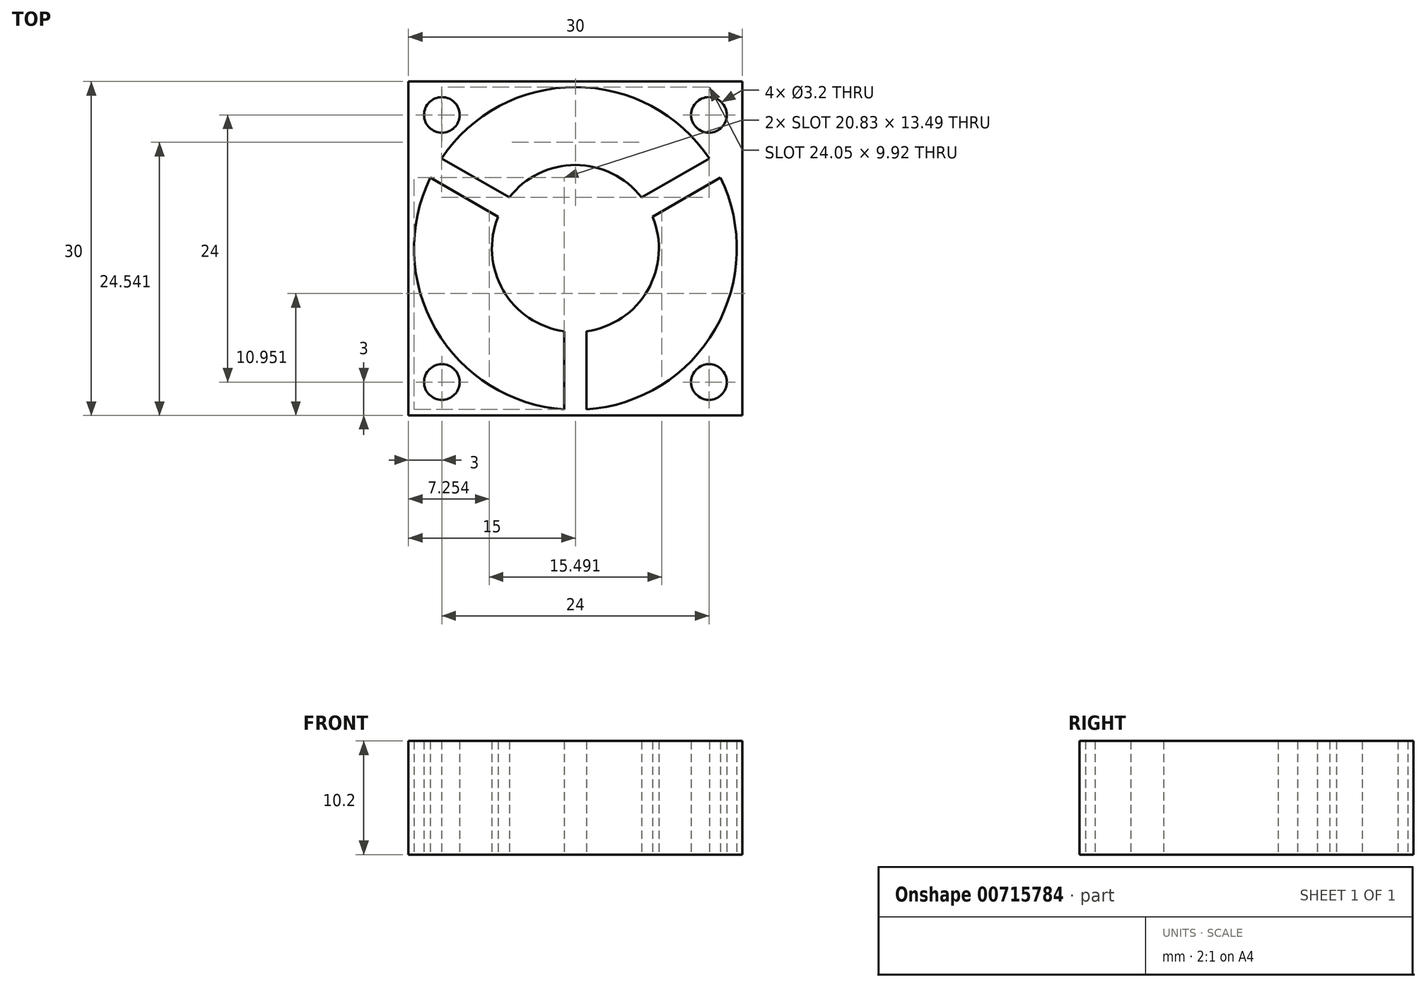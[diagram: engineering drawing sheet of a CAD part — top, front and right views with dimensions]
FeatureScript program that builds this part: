
annotation { "Feature Type Name" : "Feature", "Feature Type Description" : "" }
export const myFeature = defineFeature(function(context is Context, id is Id, definition is map)
    precondition{}
    {
        {
            var Q0;
            Q0=qCreatedBy(makeId("Top.planeOp"),FACE);
            var sketch = newSketch(context, id + "F0", { "sketchPlane" : qUnion([Q0])});
            skLineSegment(sketch, "E0.bottom", {"start": v(15, 15) * mm, "end": v(-15, 15) * mm});
            skLineSegment(sketch, "E0.top", {"start": v(15, -15) * mm, "end": v(-15, -15) * mm});
            skLineSegment(sketch, "E0.left", {"start": v(15, 15) * mm, "end": v(15, -15) * mm});
            skLineSegment(sketch, "E0.right", {"start": v(-15, 15) * mm, "end": v(-15, -15) * mm});
            skPoint(sketch, "E0.middle", {"position": v(0, 0) * mm});
            skLineSegment(sketch, "E1.bottom", {"start": v(12, 12) * mm, "end": v(-12, 12) * mm, "construction": true});
            skLineSegment(sketch, "E1.top", {"start": v(12, -12) * mm, "end": v(-12, -12) * mm, "construction": true});
            skLineSegment(sketch, "E1.left", {"start": v(12, 12) * mm, "end": v(12, -12) * mm, "construction": true});
            skLineSegment(sketch, "E1.right", {"start": v(-12, 12) * mm, "end": v(-12, -12) * mm, "construction": true});
            skCircle(sketch, "E2", {"center": v(0, 0) * mm, "radius": 14.5 * mm});
            skCircle(sketch, "E3", {"center": v(0, 0) * mm, "radius": 7.5 * mm});
            skCircle(sketch, "E4", {"center": v(-12, 12) * mm, "radius": 1.6 * mm});
            skCircle(sketch, "E5", {"center": v(12, 12) * mm, "radius": 1.6 * mm});
            skCircle(sketch, "E6", {"center": v(12, -12) * mm, "radius": 1.6 * mm});
            skCircle(sketch, "E7", {"center": v(-12, -12) * mm, "radius": 1.6 * mm});
            skLineSegment(sketch, "E8.bottom", {"start": v(1, -7.43) * mm, "end": v(-1, -7.43) * mm});
            skLineSegment(sketch, "E8.top", {"start": v(1, -14.5) * mm, "end": v(-1, -14.5) * mm});
            skLineSegment(sketch, "E8.left", {"start": v(1, -7.43) * mm, "end": v(1, -14.5) * mm});
            skLineSegment(sketch, "E8.right", {"start": v(-1, -7.43) * mm, "end": v(-1, -14.5) * mm});
            skPoint(sketch, "E8.middle", {"position": v(0, -10.97) * mm});
            skLineSegment(sketch, "E9.1.0", {"start": v(5.94, 4.58) * mm, "end": v(12.06, 8.12) * mm});
            skLineSegment(sketch, "E9.1.1", {"start": v(5.94, 4.58) * mm, "end": v(6.94, 2.85) * mm});
            skLineSegment(sketch, "E9.1.2", {"start": v(6.94, 2.85) * mm, "end": v(13.06, 6.38) * mm});
            skLineSegment(sketch, "E9.1.3", {"start": v(12.06, 8.12) * mm, "end": v(13.06, 6.38) * mm});
            skLineSegment(sketch, "E9.2.0", {"start": v(-6.94, 2.85) * mm, "end": v(-13.06, 6.38) * mm});
            skLineSegment(sketch, "E9.2.1", {"start": v(-6.94, 2.85) * mm, "end": v(-5.94, 4.58) * mm});
            skLineSegment(sketch, "E9.2.2", {"start": v(-5.94, 4.58) * mm, "end": v(-12.06, 8.12) * mm});
            skLineSegment(sketch, "E9.2.3", {"start": v(-13.06, 6.38) * mm, "end": v(-12.06, 8.12) * mm});
            skSolve(sketch);
        }
        {
            var Q0;
            Q0=makeQuery(id+"F0.imprint","IMPRINT",FACE,{"disambiguationData":[TD([[makeQuery(id+"F0.imprint","IMPRINT",EDGE,{"derivedFrom":sQuery(id+"F0.wireOp",EDGE,"E0.bottom")}),1.0]])]});
            var Q1;
            {var subQ6=sQuery(id+"F0.wireOp",EDGE,"E2");var subQ8=makeQuery(id+"F0.imprint","INTERSECT",VERTEX,{"derivedFrom":[subQ6,sQuery(id+"F0.wireOp",EDGE,"E9.1.3")]});Q1=makeQuery(id+"F0.imprint","IMPRINT",FACE,{"disambiguationData":[TD([[makeQuery(id+"F0.imprint","IMPRINT",EDGE,{"disambiguationData":[TD([[subQ8,1.0]])],"derivedFrom":subQ6}),1.0]])]});}
            var Q2;
            {var subQ4=sQuery(id+"F0.wireOp",EDGE,"E9.2.2");var subQ6=sQuery(id+"F0.wireOp",EDGE,"E2");var subQ9=makeQuery(id+"F0.imprint","INTERSECT",VERTEX,{"derivedFrom":[subQ6,subQ4]});Q2=makeQuery(id+"F0.imprint","IMPRINT",FACE,{"disambiguationData":[TD([[makeQuery(id+"F0.imprint","IMPRINT",EDGE,{"disambiguationData":[TD([[subQ9,-1.0]])],"derivedFrom":subQ6}),1.0]])]});}
            var Q3;
            {var subQ4=sQuery(id+"F0.wireOp",EDGE,"E8.right");var subQ6=sQuery(id+"F0.wireOp",EDGE,"E2");var subQ7=makeQuery(id+"F0.imprint","INTERSECT",VERTEX,{"derivedFrom":[subQ6,subQ4]});Q3=makeQuery(id+"F0.imprint","IMPRINT",FACE,{"disambiguationData":[TD([[makeQuery(id+"F0.imprint","IMPRINT",EDGE,{"disambiguationData":[TD([[subQ7,-1.0]])],"derivedFrom":subQ6}),1.0]])]});}
            var Q4;
            {var subQ0=sQuery(id+"F0.wireOp",EDGE,"E8.bottom");Q4=makeQuery(id+"F0.imprint","IMPRINT",FACE,{"disambiguationData":[TD([[makeQuery(id+"F0.imprint","IMPRINT",EDGE,{"derivedFrom":subQ0}),-1.0]])]});}
            var Q5;
            {var subQ0=sQuery(id+"F0.wireOp",EDGE,"E9.1.3");var subQ1=sQuery(id+"F0.wireOp",EDGE,"E2");var subQ2=makeQuery(id+"F0.imprint","INTERSECT",VERTEX,{"derivedFrom":[subQ1,subQ0]});Q5=makeQuery(id+"F0.imprint","IMPRINT",FACE,{"disambiguationData":[TD([[makeQuery(id+"F0.imprint","IMPRINT",EDGE,{"disambiguationData":[TD([[subQ2,1.0]])],"derivedFrom":subQ1}),-1.0]])]});}
            var Q6;
            {var subQ0=sQuery(id+"F0.wireOp",EDGE,"E8.bottom");Q6=makeQuery(id+"F0.imprint","IMPRINT",FACE,{"disambiguationData":[TD([[makeQuery(id+"F0.imprint","IMPRINT",EDGE,{"derivedFrom":subQ0}),1.0]])]});}
            var Q7;
            {var subQ0=sQuery(id+"F0.wireOp",EDGE,"E9.2.1");Q7=makeQuery(id+"F0.imprint","IMPRINT",FACE,{"disambiguationData":[TD([[makeQuery(id+"F0.imprint","IMPRINT",EDGE,{"derivedFrom":subQ0}),1.0]])]});}
            var Q8;
            {var subQ0=sQuery(id+"F0.wireOp",EDGE,"E9.1.1");Q8=makeQuery(id+"F0.imprint","IMPRINT",FACE,{"disambiguationData":[TD([[makeQuery(id+"F0.imprint","IMPRINT",EDGE,{"derivedFrom":subQ0}),1.0]])]});}
            var Q9;
            {var subQ0=sQuery(id+"F0.wireOp",EDGE,"E8.top");var subQ1=sQuery(id+"F0.wireOp",EDGE,"E2");var subQ2=makeQuery(id+"F0.imprint","INTERSECT",VERTEX,{"derivedFrom":[subQ1,subQ0]});Q9=makeQuery(id+"F0.imprint","IMPRINT",FACE,{"disambiguationData":[TD([[makeQuery(id+"F0.imprint","IMPRINT",EDGE,{"disambiguationData":[TD([[subQ2,-1.0]])],"derivedFrom":subQ1}),-1.0]])]});}
            var Q10;
            {var subQ0=sQuery(id+"F0.wireOp",EDGE,"E8.right");var subQ1=sQuery(id+"F0.wireOp",EDGE,"E2");var subQ2=makeQuery(id+"F0.imprint","INTERSECT",VERTEX,{"derivedFrom":[subQ1,subQ0]});Q10=makeQuery(id+"F0.imprint","IMPRINT",FACE,{"disambiguationData":[TD([[makeQuery(id+"F0.imprint","IMPRINT",EDGE,{"disambiguationData":[TD([[subQ2,-1.0]])],"derivedFrom":subQ1}),-1.0]])]});}
            var Q11;
            {var subQ0=sQuery(id+"F0.wireOp",EDGE,"E9.2.3");var subQ1=sQuery(id+"F0.wireOp",EDGE,"E2");var subQ2=makeQuery(id+"F0.imprint","INTERSECT",VERTEX,{"derivedFrom":[subQ1,subQ0]});Q11=makeQuery(id+"F0.imprint","IMPRINT",FACE,{"disambiguationData":[TD([[makeQuery(id+"F0.imprint","IMPRINT",EDGE,{"disambiguationData":[TD([[subQ2,-1.0]])],"derivedFrom":subQ1}),-1.0]])]});}
            var Q12;
            {var subQ0=sQuery(id+"F0.wireOp",EDGE,"E9.2.2");var subQ1=sQuery(id+"F0.wireOp",EDGE,"E2");var subQ2=makeQuery(id+"F0.imprint","INTERSECT",VERTEX,{"derivedFrom":[subQ1,subQ0]});Q12=makeQuery(id+"F0.imprint","IMPRINT",FACE,{"disambiguationData":[TD([[makeQuery(id+"F0.imprint","IMPRINT",EDGE,{"disambiguationData":[TD([[subQ2,-1.0]])],"derivedFrom":subQ1}),-1.0]])]});}
            var Q13;
            {var subQ0=sQuery(id+"F0.wireOp",EDGE,"E9.1.3");var subQ1=sQuery(id+"F0.wireOp",EDGE,"E2");var subQ2=makeQuery(id+"F0.imprint","INTERSECT",VERTEX,{"derivedFrom":[subQ1,subQ0]});Q13=makeQuery(id+"F0.imprint","IMPRINT",FACE,{"disambiguationData":[TD([[makeQuery(id+"F0.imprint","IMPRINT",EDGE,{"disambiguationData":[TD([[subQ2,-1.0]])],"derivedFrom":subQ1}),-1.0]])]});}
            extrude(context, id + "F1", {"entities" : qUnion([Q0, Q1, Q2, Q3, Q4, Q5, Q6, Q7, Q8, Q9, Q10, Q11, Q12, Q13]), "depth" : 10.2 * mm});
        }
    });
